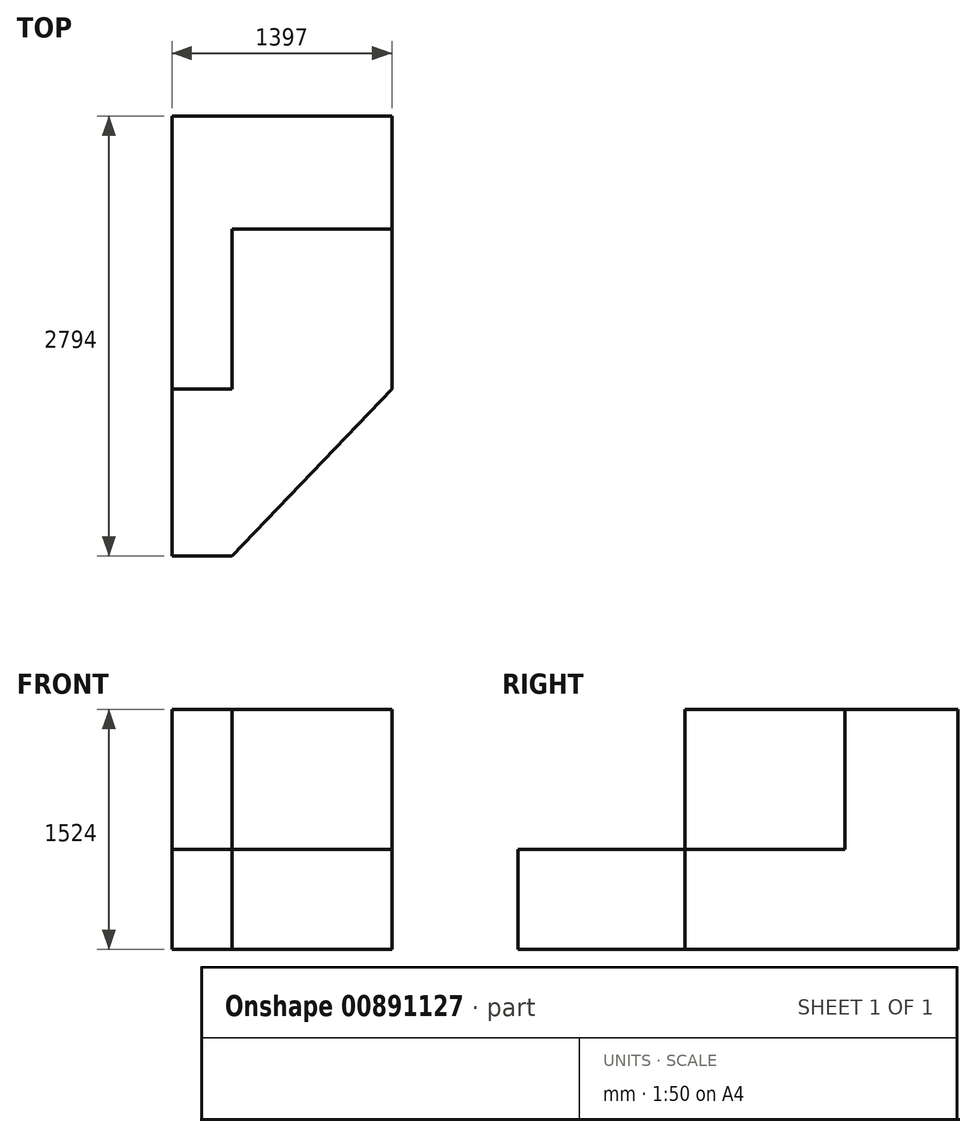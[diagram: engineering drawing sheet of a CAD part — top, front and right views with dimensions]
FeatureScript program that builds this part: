
annotation { "Feature Type Name" : "Feature", "Feature Type Description" : "" }
export const myFeature = defineFeature(function(context is Context, id is Id, definition is map)
    precondition{}
    {
        {
            var Q0;
            Q0=qCreatedBy(makeId("Top.planeOp"),FACE);
            var sketch = newSketch(context, id + "F0", { "sketchPlane" : qUnion([Q0])});
            skLineSegment(sketch, "E0.bottom", {"start": v(0, 0) * mm, "end": v(-1397, 0) * mm});
            skLineSegment(sketch, "E0.top", {"start": v(0, -2794) * mm, "end": v(-1397, -2794) * mm});
            skLineSegment(sketch, "E0.left", {"start": v(0, 0) * mm, "end": v(0, -2794) * mm});
            skLineSegment(sketch, "E0.right", {"start": v(-1397, 0) * mm, "end": v(-1397, -2794) * mm});
            skSolve(sketch);
        }
        {
            var Q0;
            Q0 = qSketchRegion(id + "F0", true);
            extrude(context, id + "F1", {"entities" : qUnion([Q0]), "depth" : 635 * mm, "offsetDistance" : 25.4 * mm});
        }
        {
            var Q0;
            Q0=makeQuery(id+"F1.opExtrude","CAP_FACE",FACE,{"disambiguationData":[OSD([sQuery(id+"F0.wireOp",EDGE,"E0.bottom"),sQuery(id+"F0.wireOp",EDGE,"E0.top"),sQuery(id+"F0.wireOp",EDGE,"E0.left"),sQuery(id+"F0.wireOp",EDGE,"E0.right")])],"isStart":false});
            var sketch = newSketch(context, id + "F2", { "sketchPlane" : qUnion([Q0])});
            skLineSegment(sketch, "E1.bottom", {"start": v(-1397, 0) * mm, "end": v(0, 0) * mm});
            skLineSegment(sketch, "E1.top", {"start": v(-1397, -716.89) * mm, "end": v(0, -716.89) * mm});
            skLineSegment(sketch, "E1.left", {"start": v(-1397, 0) * mm, "end": v(-1397, -716.89) * mm});
            skLineSegment(sketch, "E1.right", {"start": v(0, 0) * mm, "end": v(0, -716.89) * mm});
            skSolve(sketch);
        }
        {
            var Q0;
            Q0 = qSketchRegion(id + "F2", true);
            extrude(context, id + "F3", {"entities" : qUnion([Q0]), "operationType" : NewBodyOperationType.ADD, "depth" : 889 * mm, "offsetDistance" : 25.4 * mm});
        }
        {
            var Q0;
            Q0=makeQuery(id+"F1.opExtrude","CAP_FACE",FACE,{"disambiguationData":[OSD([sQuery(id+"F0.wireOp",EDGE,"E0.bottom"),sQuery(id+"F0.wireOp",EDGE,"E0.top"),sQuery(id+"F0.wireOp",EDGE,"E0.left"),sQuery(id+"F0.wireOp",EDGE,"E0.right")])],"isStart":false});
            var sketch = newSketch(context, id + "F4", { "sketchPlane" : qUnion([Q0])});
            skLineSegment(sketch, "E2.bottom", {"start": v(-1397, -716.89) * mm, "end": v(-1016, -716.89) * mm});
            skLineSegment(sketch, "E2.top", {"start": v(-1397, -1732.89) * mm, "end": v(-1016, -1732.89) * mm});
            skLineSegment(sketch, "E2.left", {"start": v(-1397, -716.89) * mm, "end": v(-1397, -1732.89) * mm});
            skLineSegment(sketch, "E2.right", {"start": v(-1016, -716.89) * mm, "end": v(-1016, -1732.89) * mm});
            skSolve(sketch);
        }
        {
            var Q0;
            Q0 = qSketchRegion(id + "F4", true);
            extrude(context, id + "F5", {"entities" : qUnion([Q0]), "operationType" : NewBodyOperationType.ADD, "depth" : 889 * mm, "offsetDistance" : 25.4 * mm});
        }
        {
            var Q0;
            Q0=makeQuery(id+"F1.opExtrude","CAP_FACE",FACE,{"disambiguationData":[OSD([sQuery(id+"F0.wireOp",EDGE,"E0.bottom"),sQuery(id+"F0.wireOp",EDGE,"E0.top"),sQuery(id+"F0.wireOp",EDGE,"E0.left"),sQuery(id+"F0.wireOp",EDGE,"E0.right")])],"isStart":false});
            var sketch = newSketch(context, id + "F6", { "sketchPlane" : qUnion([Q0])});
            skLineSegment(sketch, "E3", {"start": v(-1016, -1732.89) * mm, "end": v(0, -1732.89) * mm});
            skLineSegment(sketch, "E4", {"start": v(-1016, -1732.89) * mm, "end": v(-1016, -2794) * mm});
            skLineSegment(sketch, "E5", {"start": v(-1016, -2794) * mm, "end": v(0, -1732.89) * mm});
            skSolve(sketch);
        }
        {
            var Q0;
            {var subQ0=sQuery(id+"F6.wireOp",EDGE,"E5");Q0=makeQuery(id+"F6.imprint","IMPRINT",FACE,{"disambiguationData":[TD([[makeQuery(id+"F6.imprint","IMPRINT",EDGE,{"derivedFrom":subQ0}),-1.0]])]});}
            extrude(context, id + "F7", {"entities" : qUnion([Q0]), "operationType" : NewBodyOperationType.REMOVE, "oppositeDirection" : true, "depth" : 635 * mm, "offsetDistance" : 25.4 * mm});
        }
    });
